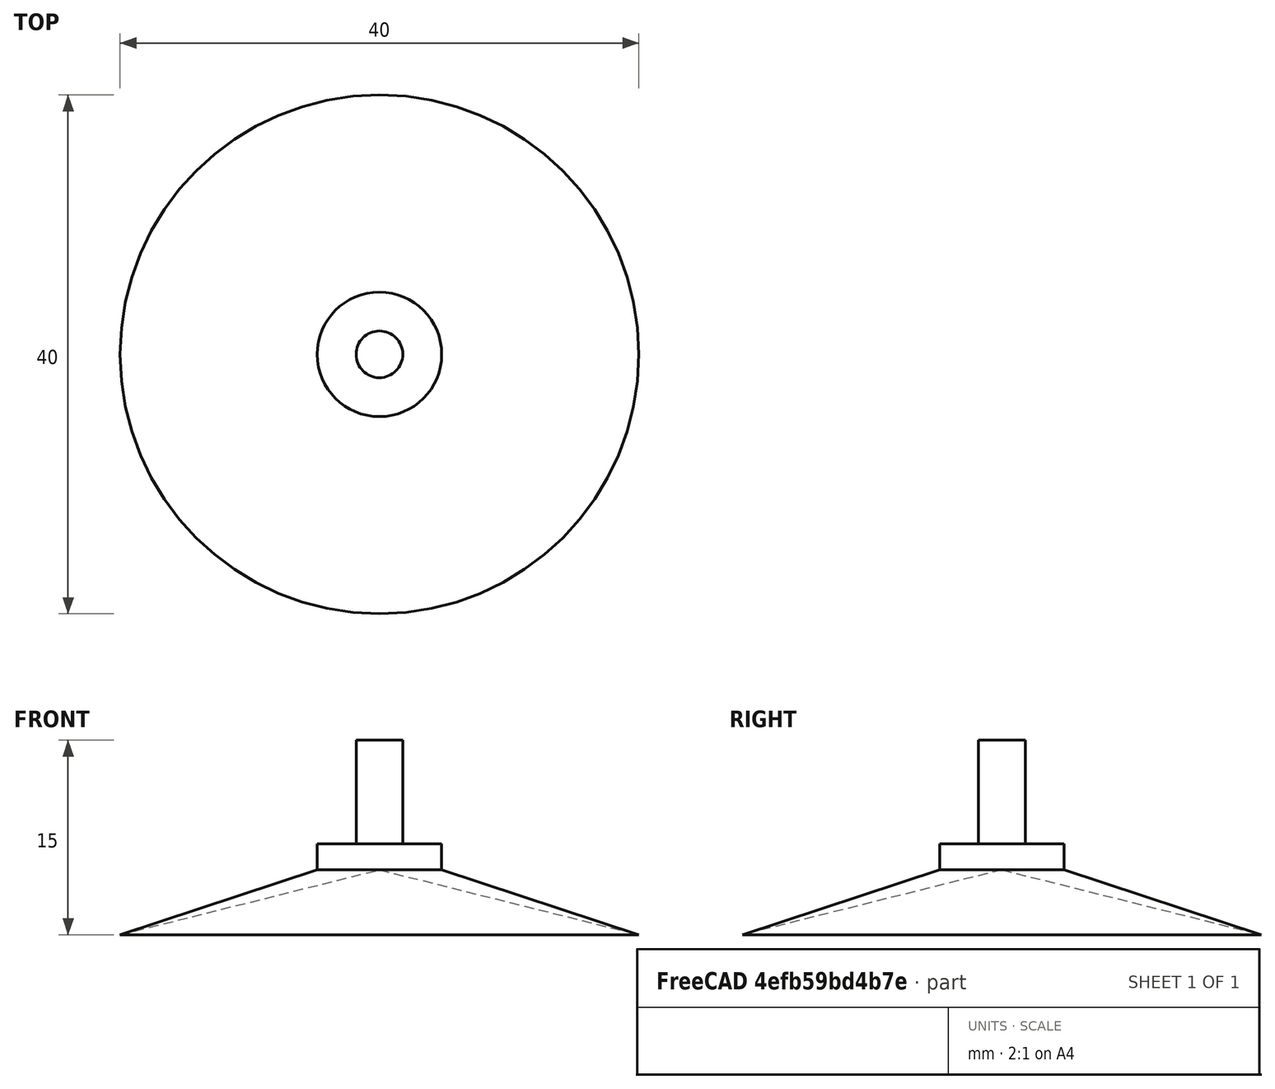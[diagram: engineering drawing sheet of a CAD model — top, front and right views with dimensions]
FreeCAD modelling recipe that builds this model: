
FCSTD DOCUMENT  (FreeCAD 0.16R6151 (Git))
Label: Sucker
License: All rights reserved
LicenseURL: http://en.wikipedia.org/wiki/All_rights_reserved
objects: Sketcher::SketchObject×1, PartDesign::Revolution×1
note: 3 computed .brp shape members not serialized (recipe doc carries the construction recipe); baked Part::Feature solids carry a one-line shape summary decoded from their .brp

FEATURE [Sketcher::SketchObject] Sketch
  Placement = pos=(0,0,0) rot=(-1,0,0;4.71239rad)
  sketch-geometry (8):
    g0: LineSegment StartX=0 StartY=15 StartZ=0 EndX=-1.8 EndY=15 EndZ=0
    g1: LineSegment StartX=-1.8 StartY=15 StartZ=0 EndX=-1.8 EndY=7 EndZ=0
    g2: LineSegment StartX=-1.8 StartY=7 StartZ=0 EndX=-4.8 EndY=7 EndZ=0
    g3: LineSegment StartX=-4.8 StartY=7 StartZ=0 EndX=-4.8 EndY=5 EndZ=0
    g4: LineSegment StartX=-4.8 StartY=5 StartZ=0 EndX=-20 EndY=0 EndZ=0
    g5: LineSegment StartX=-20 StartY=0 StartZ=0 EndX=0 EndY=5 EndZ=0
    g6: LineSegment StartX=0 StartY=5 StartZ=0 EndX=0 EndY=15 EndZ=0
    g7: LineSegment [constr] StartX=-4.8 StartY=5 StartZ=0 EndX=0 EndY=5 EndZ=0
  constraints (23):
    c: PointOnObject(g0,g-2)
    c: Horizontal(g0)
    c: Coincident(g0,g1)
    c: Vertical(g1)
    c: Coincident(g1,g2)
    c: Horizontal(g2)
    c: Coincident(g2,g3)
    c: Vertical(g3)
    c: Coincident(g3,g4)
    c: PointOnObject(g4,g-1)
    c: Coincident(g4,g5)
    c: PointOnObject(g5,g-2)
    c: Coincident(g5,g6)
    c: Coincident(g6,g0)
    c: DistanceX(g0) = -1.8
    c: DistanceX(g2) = -3
    c: Coincident(g7,g3)
    c: Coincident(g7,g5)
    c: Horizontal(g7)
    c: DistanceX(g-1,g4) = -20
    c: DistanceY(g1) = -8
    c: DistanceY(g3) = -2
    c: DistanceY(g-1,g0) = 15
FEATURE [PartDesign::Revolution] Revolution
  Angle = 360
  Axis = (0,0,1)
  Base = (0,0,0)
  Placement = pos=(0,0,0) rot=(-1,0,0;4.71239rad)
  ReferenceAxis = -> Sketch [V_Axis]
  Sketch = -> Sketch
